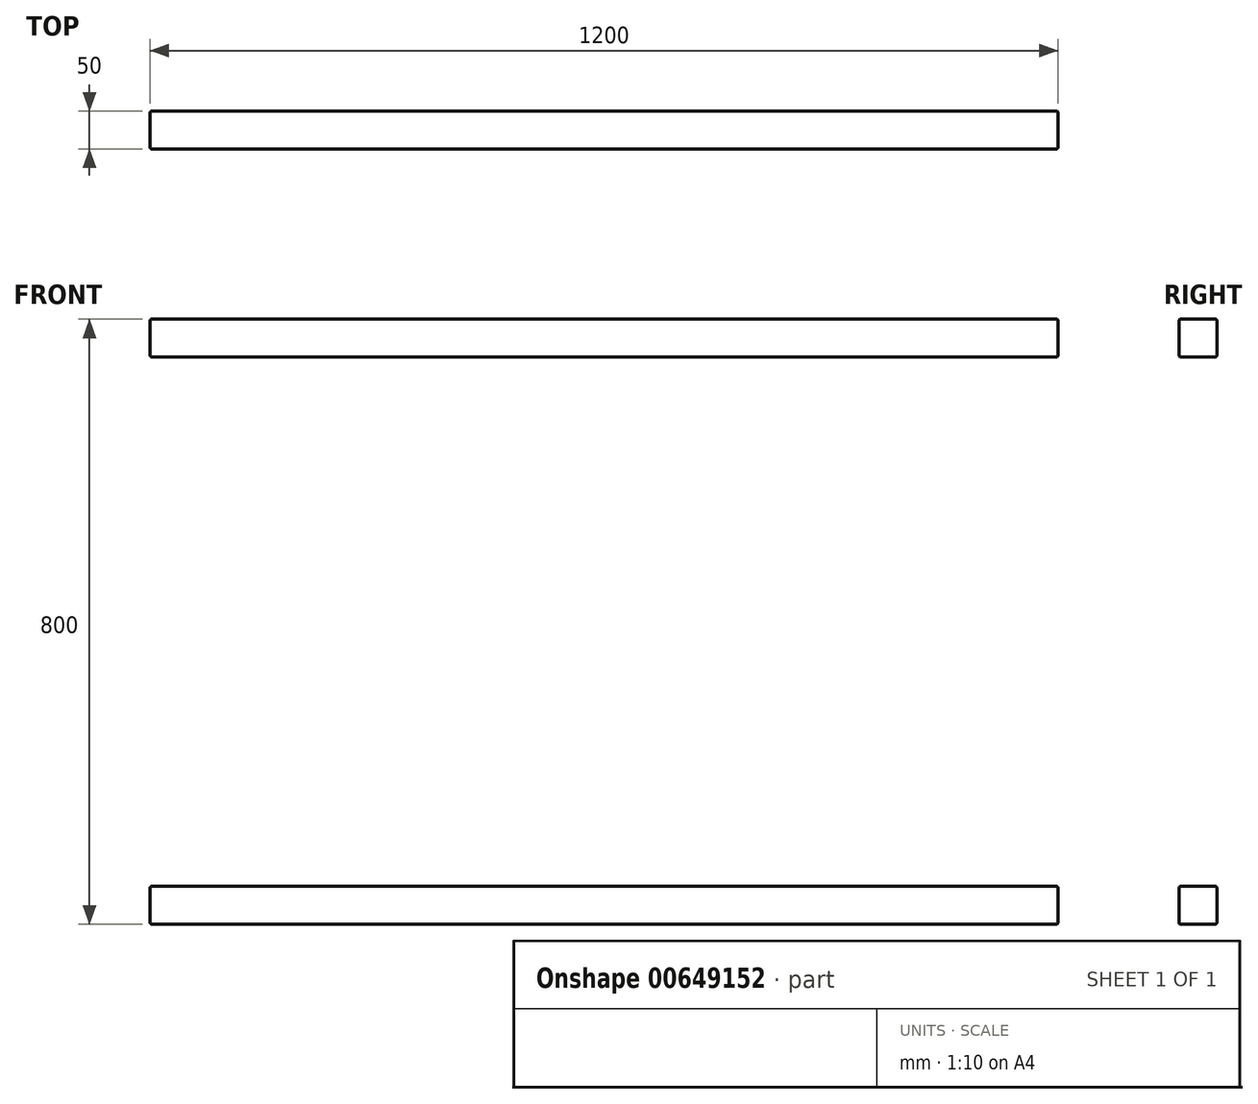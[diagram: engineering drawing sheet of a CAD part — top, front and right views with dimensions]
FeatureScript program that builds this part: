
annotation { "Feature Type Name" : "Feature", "Feature Type Description" : "" }
export const myFeature = defineFeature(function(context is Context, id is Id, definition is map)
    precondition{}
    {
        {
            var Q0;
            Q0=qCreatedBy(makeId("Front.planeOp"),FACE);
            var sketch = newSketch(context, id + "F0", { "sketchPlane" : qUnion([Q0])});
            skLineSegment(sketch, "E0.bottom", {"start": v(0, 0) * mm, "end": v(1200, 0) * mm});
            skLineSegment(sketch, "E0.top", {"start": v(0, -50) * mm, "end": v(1200, -50) * mm});
            skLineSegment(sketch, "E0.left", {"start": v(0, 0) * mm, "end": v(0, -50) * mm});
            skLineSegment(sketch, "E0.right", {"start": v(1200, 0) * mm, "end": v(1200, -50) * mm});
            skLineSegment(sketch, "E1.bottom", {"start": v(1200, -50) * mm, "end": v(1150, -50) * mm});
            skLineSegment(sketch, "E1.top", {"start": v(1200, -750) * mm, "end": v(1150, -750) * mm});
            skLineSegment(sketch, "E1.left", {"start": v(1200, -50) * mm, "end": v(1200, -750) * mm});
            skLineSegment(sketch, "E1.right", {"start": v(1150, -50) * mm, "end": v(1150, -750) * mm});
            skLineSegment(sketch, "E2.top", {"start": v(0, -50) * mm, "end": v(50, -50) * mm});
            skLineSegment(sketch, "E3.bottom", {"start": v(1200, -750) * mm, "end": v(0, -750) * mm});
            skLineSegment(sketch, "E3.top", {"start": v(1200, -800) * mm, "end": v(0, -800) * mm});
            skLineSegment(sketch, "E3.left", {"start": v(1200, -750) * mm, "end": v(1200, -800) * mm});
            skLineSegment(sketch, "E3.right", {"start": v(0, -750) * mm, "end": v(0, -800) * mm});
            skLineSegment(sketch, "E4.bottom", {"start": v(0, -750) * mm, "end": v(50, -750) * mm});
            skLineSegment(sketch, "E4.left", {"start": v(0, -750) * mm, "end": v(0, -50) * mm});
            skLineSegment(sketch, "E4.right", {"start": v(50, -750) * mm, "end": v(50, -50) * mm});
            skSolve(sketch);
        }
        {
            var Q0;
            Q0=makeQuery(id+"F0.imprint","IMPRINT",FACE,{"disambiguationData":[TD([[makeQuery(id+"F0.imprint","IMPRINT",EDGE,{"derivedFrom":sQuery(id+"F0.wireOp",EDGE,"E0.bottom")}),-1.0]])]});
            var Q1;
            Q1=makeQuery(id+"F0.imprint","IMPRINT",FACE,{"disambiguationData":[TD([[makeQuery(id+"F0.imprint","IMPRINT",EDGE,{"derivedFrom":sQuery(id+"F0.wireOp",EDGE,"E4.bottom")}),1.0]])]});
            var Q2;
            Q2=makeQuery(id+"F0.imprint","IMPRINT",FACE,{"disambiguationData":[TD([[makeQuery(id+"F0.imprint","IMPRINT",EDGE,{"derivedFrom":sQuery(id+"F0.wireOp",EDGE,"E3.top")}),-1.0]])]});
            var Q3;
            Q3=makeQuery(id+"F0.imprint","IMPRINT",FACE,{"disambiguationData":[TD([[makeQuery(id+"F0.imprint","IMPRINT",EDGE,{"derivedFrom":sQuery(id+"F0.wireOp",EDGE,"E1.bottom")}),1.0]])]});
            extrude(context, id + "F1", {"entities" : qUnion([Q0, Q1, Q2, Q3]), "depth" : 50 * mm, "offsetDistance" : 25 * mm});
        }
        {
            var Q0;
            Q0=makeQuery(id+"F1.opExtrude","CAP_EDGE",EDGE,{"disambiguationData":[OSD([sQuery(id+"F0.wireOp",EDGE,"E0.bottom")])],"isStart":false});
            var Q1;
            Q1=makeQuery(id+"F1.opExtrude","SWEPT_EDGE",EDGE,{"disambiguationData":[OSD([sQuery(id+"F0.wireOp",EDGE,"E0.bottom"),sQuery(id+"F0.wireOp",EDGE,"E0.right")])]});
            var Q2;
            Q2=makeQuery(id+"F1.opExtrude","CAP_EDGE",EDGE,{"disambiguationData":[OSD([sQuery(id+"F0.wireOp",EDGE,"E0.right"),sQuery(id+"F0.wireOp",EDGE,"E1.left"),sQuery(id+"F0.wireOp",EDGE,"E3.left")])],"isStart":false});
            var Q3;
            Q3=makeQuery(id+"F1.opExtrude","CAP_EDGE",EDGE,{"disambiguationData":[OSD([sQuery(id+"F0.wireOp",EDGE,"E0.right"),sQuery(id+"F0.wireOp",EDGE,"E1.left"),sQuery(id+"F0.wireOp",EDGE,"E3.left")])],"isStart":true});
            var Q4;
            Q4=makeQuery(id+"F1.opExtrude","CAP_FACE",FACE,{"disambiguationData":[OSD([sQuery(id+"F0.wireOp",EDGE,"E0.bottom"),sQuery(id+"F0.wireOp",EDGE,"E0.top"),sQuery(id+"F0.wireOp",EDGE,"E0.left"),sQuery(id+"F0.wireOp",EDGE,"E0.right"),sQuery(id+"F0.wireOp",EDGE,"E1.left"),sQuery(id+"F0.wireOp",EDGE,"E1.right"),sQuery(id+"F0.wireOp",EDGE,"E3.bottom"),sQuery(id+"F0.wireOp",EDGE,"E3.top"),sQuery(id+"F0.wireOp",EDGE,"E3.left"),sQuery(id+"F0.wireOp",EDGE,"E3.right"),sQuery(id+"F0.wireOp",EDGE,"E4.left"),sQuery(id+"F0.wireOp",EDGE,"E4.right")])],"isStart":true});
            var Q5;
            Q5=makeQuery(id+"F1.opExtrude","SWEPT_FACE",FACE,{"disambiguationData":[OSD([sQuery(id+"F0.wireOp",EDGE,"E0.top")])]});
            var Q6;
            Q6=makeQuery(id+"F1.opExtrude","SWEPT_FACE",FACE,{"disambiguationData":[OSD([sQuery(id+"F0.wireOp",EDGE,"E3.bottom")])]});
            var Q7;
            Q7=makeQuery(id+"F1.opExtrude","SWEPT_FACE",FACE,{"disambiguationData":[OSD([sQuery(id+"F0.wireOp",EDGE,"E3.top")])]});
            var Q8;
            Q8=makeQuery(id+"F1.opExtrude","SWEPT_FACE",FACE,{"disambiguationData":[OSD([sQuery(id+"F0.wireOp",EDGE,"E0.left"),sQuery(id+"F0.wireOp",EDGE,"E3.right"),sQuery(id+"F0.wireOp",EDGE,"E4.left")])]});
            fillet(context, id + "F2", {"entities" : qUnion([Q0, Q1, Q2, Q3, Q4, Q5, Q6, Q7, Q8]), "radius" : 2 * mm, "tangentPropagation" : true, "allowEdgeOverflow" : false});
        }
    });
